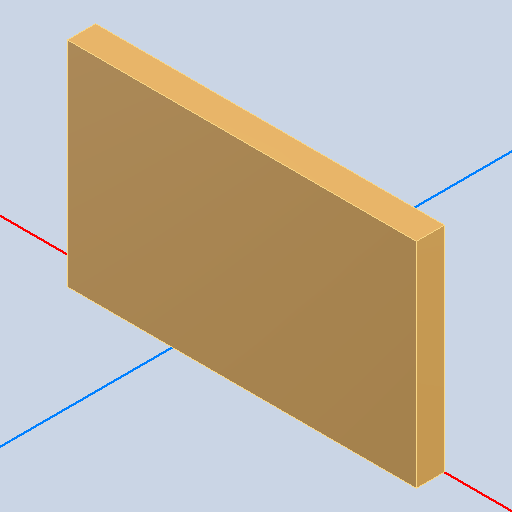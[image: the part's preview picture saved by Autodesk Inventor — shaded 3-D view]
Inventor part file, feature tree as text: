
AUTODESK INVENTOR PART (.ipt)
format: ipt  version: 2022 (Build 260153000, 153)  size: 91,648 bytes
history: native  units: mm
features: other x2, extrude x1
ambient origin geometry x8: Origin, YZ Plane, XZ Plane, XY Plane, X Axis, Y Axis, Z Axis, Center Point
bodies: Body1 (feature_tree)
feature tree (3):
  other  "Твердое тело1"
  extrude  "Выдавливание1"  Depth=1.0mm TaperAngle=0.0deg
  other  "SCREWTERMINAL-5MM-2, J2_SCREWTERMINAL-5MM-2_6"
